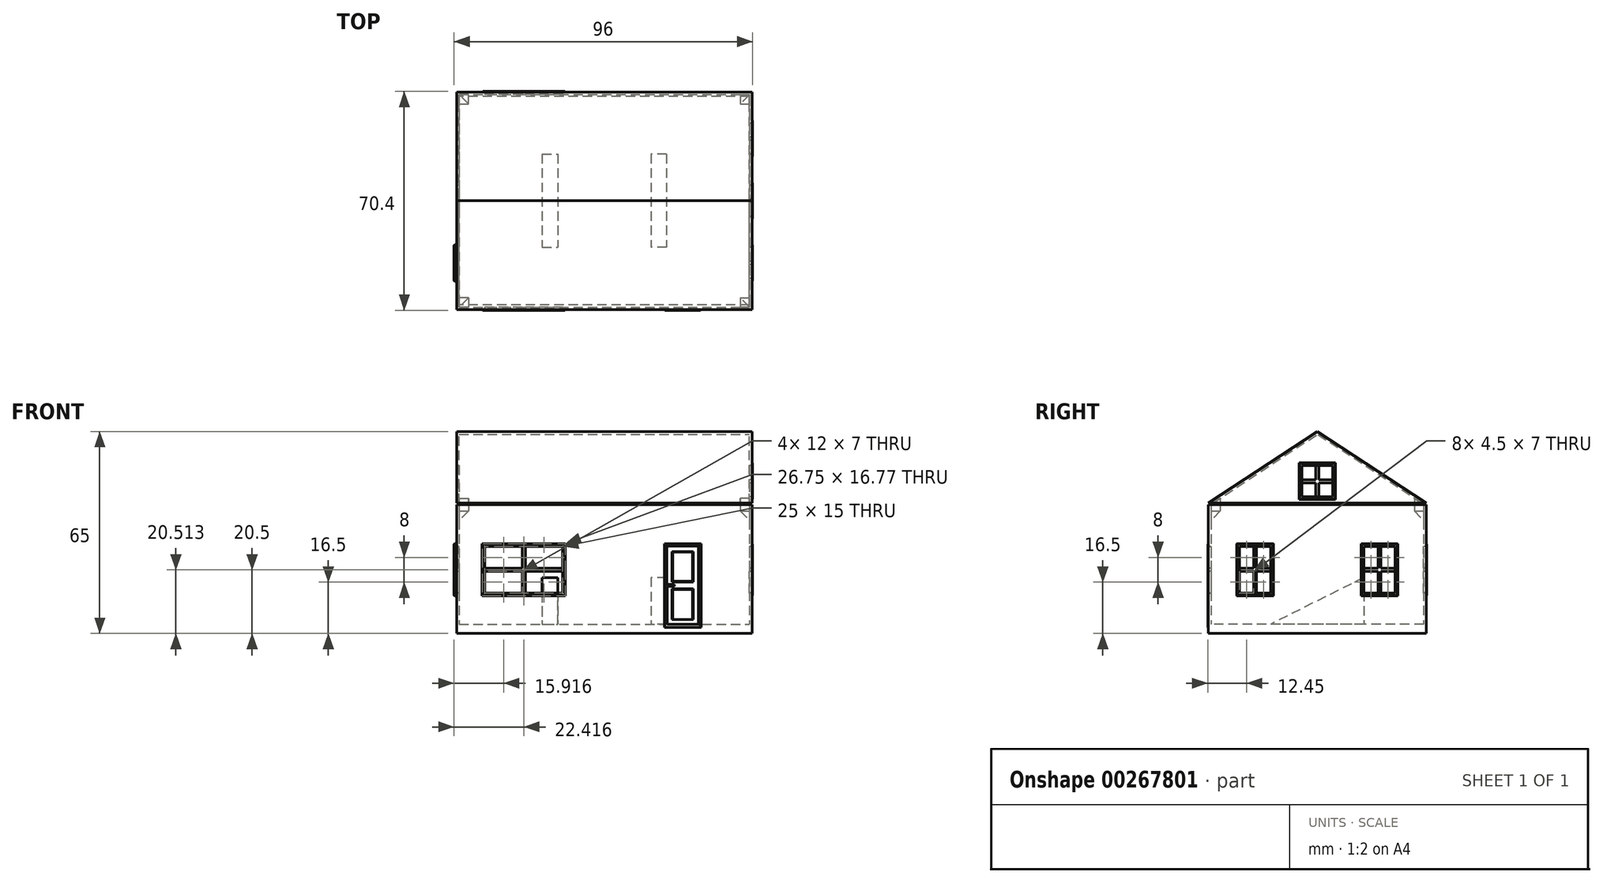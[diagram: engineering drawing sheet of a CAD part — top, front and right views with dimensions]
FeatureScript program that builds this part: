
annotation { "Feature Type Name" : "Feature", "Feature Type Description" : "" }
export const myFeature = defineFeature(function(context is Context, id is Id, definition is map)
    precondition{}
    {
        {
            var Q0;
            Q0=qCreatedBy(makeId("Top.planeOp"),FACE);
            var sketch = newSketch(context, id + "F0", { "sketchPlane" : qUnion([Q0])});
            skLineSegment(sketch, "E0.bottom", {"start": v(-47.5, 35) * mm, "end": v(47.5, 35) * mm});
            skLineSegment(sketch, "E0.top", {"start": v(-47.5, -35) * mm, "end": v(47.5, -35) * mm});
            skLineSegment(sketch, "E0.left", {"start": v(-47.5, 35) * mm, "end": v(-47.5, -35) * mm});
            skLineSegment(sketch, "E0.right", {"start": v(47.5, 35) * mm, "end": v(47.5, -35) * mm});
            skPoint(sketch, "E0.middle", {"position": v(0, 0) * mm});
            skLineSegment(sketch, "E1.bottom", {"start": v(57.5, 45) * mm, "end": v(-57.5, 45) * mm});
            skLineSegment(sketch, "E1.top", {"start": v(57.5, -45) * mm, "end": v(-57.5, -45) * mm});
            skLineSegment(sketch, "E1.left", {"start": v(57.5, 45) * mm, "end": v(57.5, -45) * mm});
            skLineSegment(sketch, "E1.right", {"start": v(-57.5, 45) * mm, "end": v(-57.5, -45) * mm});
            skLineSegment(sketch, "E2.0", {"start": v(-49.5, 37) * mm, "end": v(-49.5, -37) * mm});
            skLineSegment(sketch, "E2.1", {"start": v(-49.5, 37) * mm, "end": v(49.5, 37) * mm});
            skLineSegment(sketch, "E2.2", {"start": v(49.5, 37) * mm, "end": v(49.5, -37) * mm});
            skLineSegment(sketch, "E2.3", {"start": v(-49.5, -37) * mm, "end": v(49.5, -37) * mm});
            skSolve(sketch);
        }
        {
            var Q0;
            Q0=makeQuery(id+"F0.imprint","IMPRINT",FACE,{"disambiguationData":[TD([[makeQuery(id+"F0.imprint","IMPRINT",EDGE,{"derivedFrom":sQuery(id+"F0.wireOp",EDGE,"E0.bottom")}),-1.0]])]});
            extrude(context, id + "F1", {"entities" : qUnion([Q0]), "depth" : 65 * mm});
        }
        {
            var Q0;
            Q0=makeQuery(id+"F1.opExtrude","SWEPT_FACE",FACE,{"disambiguationData":[OSD([sQuery(id+"F0.wireOp",EDGE,"E0.left")])]});
            var sketch = newSketch(context, id + "F2", { "sketchPlane" : qUnion([Q0])});
            skLineSegment(sketch, "E3", {"start": v(0, 65) * mm, "end": v(35, 42) * mm});
            skLineSegment(sketch, "E4", {"start": v(0, 65) * mm, "end": v(0, 42.56) * mm});
            skLineSegment(sketch, "E5.MirrorCS", {"start": v(0, 65) * mm, "end": v(-35, 42) * mm});
            skLineSegment(sketch, "E6", {"start": v(-35, 42) * mm, "end": v(-35, 65) * mm});
            skLineSegment(sketch, "E7", {"start": v(-35, 65) * mm, "end": v(35, 65) * mm});
            skLineSegment(sketch, "E8", {"start": v(35, 65) * mm, "end": v(35, 42) * mm});
            skSolve(sketch);
        }
        {
            var Q0;
            Q0 = qSketchRegion(id + "F2", true);
            extrude(context, id + "F3", {"entities" : qUnion([Q0]), "operationType" : NewBodyOperationType.REMOVE, "oppositeDirection" : true, "depth" : 102.4 * mm});
        }
        {
            var Q0;
            Q0=makeQuery(id+"F1.opExtrude","SWEPT_FACE",FACE,{"disambiguationData":[OSD([sQuery(id+"F0.wireOp",EDGE,"E0.left")])]});
            var sketch = newSketch(context, id + "F4", { "sketchPlane" : qUnion([Q0])});
            skLineSegment(sketch, "E9.bottom", {"start": v(-15, 13) * mm, "end": v(-25, 13) * mm});
            skLineSegment(sketch, "E9.top", {"start": v(-15, 28) * mm, "end": v(-25, 28) * mm});
            skLineSegment(sketch, "E9.left", {"start": v(-15, 13) * mm, "end": v(-15, 28) * mm});
            skLineSegment(sketch, "E9.right", {"start": v(-25, 13) * mm, "end": v(-25, 28) * mm});
            skPoint(sketch, "E9.middle", {"position": v(-20, 20.5) * mm});
            skLineSegment(sketch, "E10.bottom", {"start": v(-19.5, 28) * mm, "end": v(-20.5, 28) * mm});
            skLineSegment(sketch, "E10.top", {"start": v(-19.5, 13) * mm, "end": v(-20.5, 13) * mm});
            skLineSegment(sketch, "E10.left", {"start": v(-19.5, 28) * mm, "end": v(-19.5, 13) * mm});
            skLineSegment(sketch, "E10.right", {"start": v(-20.5, 28) * mm, "end": v(-20.5, 13) * mm});
            skLineSegment(sketch, "E11.bottom", {"start": v(-15, 21) * mm, "end": v(-25, 21) * mm});
            skLineSegment(sketch, "E11.top", {"start": v(-15, 20) * mm, "end": v(-25, 20) * mm});
            skLineSegment(sketch, "E11.left", {"start": v(-15, 21) * mm, "end": v(-15, 20) * mm});
            skLineSegment(sketch, "E11.right", {"start": v(-25, 21) * mm, "end": v(-25, 20) * mm});
            skLineSegment(sketch, "E12.bottom", {"start": v(-14, 29) * mm, "end": v(-26, 29) * mm});
            skLineSegment(sketch, "E12.top", {"start": v(-14, 12) * mm, "end": v(-26, 12) * mm});
            skLineSegment(sketch, "E12.left", {"start": v(-14, 29) * mm, "end": v(-14, 12) * mm});
            skLineSegment(sketch, "E12.right", {"start": v(-26, 29) * mm, "end": v(-26, 12) * mm});
            skLineSegment(sketch, "E13", {"start": v(0, 65) * mm, "end": v(0, 3) * mm});
            skLineSegment(sketch, "E14.MirrorCS", {"start": v(14, 29) * mm, "end": v(26, 29) * mm});
            skLineSegment(sketch, "E15.MirrorCS", {"start": v(26, 29) * mm, "end": v(26, 12) * mm});
            skLineSegment(sketch, "E16.MirrorCS", {"start": v(25, 13) * mm, "end": v(25, 28) * mm});
            skLineSegment(sketch, "E17.MirrorCS", {"start": v(15, 21) * mm, "end": v(25, 21) * mm});
            skLineSegment(sketch, "E18.MirrorCS", {"start": v(15, 20) * mm, "end": v(25, 20) * mm});
            skLineSegment(sketch, "E19.MirrorCS", {"start": v(20.5, 28) * mm, "end": v(20.5, 13) * mm});
            skLineSegment(sketch, "E20.MirrorCS", {"start": v(15, 13) * mm, "end": v(25, 13) * mm});
            skLineSegment(sketch, "E21.MirrorCS", {"start": v(14, 12) * mm, "end": v(26, 12) * mm});
            skLineSegment(sketch, "E22.MirrorCS", {"start": v(15, 13) * mm, "end": v(15, 28) * mm});
            skLineSegment(sketch, "E23.MirrorCS", {"start": v(14, 29) * mm, "end": v(14, 12) * mm});
            skLineSegment(sketch, "E24.MirrorCS", {"start": v(15, 28) * mm, "end": v(25, 28) * mm});
            skLineSegment(sketch, "E25.MirrorCS", {"start": v(19.5, 28) * mm, "end": v(19.5, 13) * mm});
            skLineSegment(sketch, "E26.bottom", {"start": v(-5, 54) * mm, "end": v(5, 54) * mm});
            skLineSegment(sketch, "E26.top", {"start": v(-5, 44) * mm, "end": v(5, 44) * mm});
            skLineSegment(sketch, "E26.left", {"start": v(-5, 54) * mm, "end": v(-5, 44) * mm});
            skLineSegment(sketch, "E26.right", {"start": v(5, 54) * mm, "end": v(5, 44) * mm});
            skPoint(sketch, "E26.middle", {"position": v(0, 49) * mm});
            skLineSegment(sketch, "E27.bottom", {"start": v(0.5, 54) * mm, "end": v(-0.5, 54) * mm});
            skLineSegment(sketch, "E27.top", {"start": v(0.5, 44) * mm, "end": v(-0.5, 44) * mm});
            skLineSegment(sketch, "E27.left", {"start": v(0.5, 54) * mm, "end": v(0.5, 44) * mm});
            skLineSegment(sketch, "E27.right", {"start": v(-0.5, 54) * mm, "end": v(-0.5, 44) * mm});
            skLineSegment(sketch, "E28.bottom", {"start": v(5, 49.5) * mm, "end": v(-5, 49.5) * mm});
            skLineSegment(sketch, "E28.top", {"start": v(5, 48.5) * mm, "end": v(-5, 48.5) * mm});
            skLineSegment(sketch, "E28.left", {"start": v(5, 49.5) * mm, "end": v(5, 48.5) * mm});
            skLineSegment(sketch, "E28.right", {"start": v(-5, 49.5) * mm, "end": v(-5, 48.5) * mm});
            skLineSegment(sketch, "E29.bottom", {"start": v(6, 55) * mm, "end": v(-6, 55) * mm});
            skLineSegment(sketch, "E29.top", {"start": v(6, 43) * mm, "end": v(-6, 43) * mm});
            skLineSegment(sketch, "E29.left", {"start": v(6, 55) * mm, "end": v(6, 43) * mm});
            skLineSegment(sketch, "E29.right", {"start": v(-6, 55) * mm, "end": v(-6, 43) * mm});
            skSolve(sketch);
        }
        {
            var Q0;
            {var subQ0=sQuery(id+"F4.wireOp",EDGE,"E26.left");var subQ1=sQuery(id+"F4.wireOp",EDGE,"E26.bottom");var subQ2=makeQuery(id+"F4.imprint","INTERSECT",VERTEX,{"derivedFrom":[subQ1,subQ0]});Q0=makeQuery(id+"F4.imprint","IMPRINT",FACE,{"disambiguationData":[TD([[makeQuery(id+"F4.imprint","IMPRINT",EDGE,{"disambiguationData":[TD([[subQ2,-1.0]])],"derivedFrom":subQ1}),-1.0]])]});}
            var Q1;
            {var subQ0=sQuery(id+"F4.wireOp",EDGE,"E26.left");var subQ1=sQuery(id+"F4.wireOp",EDGE,"E26.top");var subQ2=makeQuery(id+"F4.imprint","INTERSECT",VERTEX,{"derivedFrom":[subQ1,subQ0]});Q1=makeQuery(id+"F4.imprint","IMPRINT",FACE,{"disambiguationData":[TD([[makeQuery(id+"F4.imprint","IMPRINT",EDGE,{"disambiguationData":[TD([[subQ2,-1.0]])],"derivedFrom":subQ1}),1.0]])]});}
            var Q2;
            {var subQ0=sQuery(id+"F4.wireOp",EDGE,"E26.right");var subQ1=sQuery(id+"F4.wireOp",EDGE,"E26.bottom");var subQ2=makeQuery(id+"F4.imprint","INTERSECT",VERTEX,{"derivedFrom":[subQ1,subQ0]});Q2=makeQuery(id+"F4.imprint","IMPRINT",FACE,{"disambiguationData":[TD([[makeQuery(id+"F4.imprint","IMPRINT",EDGE,{"disambiguationData":[TD([[subQ2,1.0]])],"derivedFrom":subQ1}),-1.0]])]});}
            var Q3;
            {var subQ0=sQuery(id+"F4.wireOp",EDGE,"E26.right");var subQ1=sQuery(id+"F4.wireOp",EDGE,"E26.top");var subQ2=makeQuery(id+"F4.imprint","INTERSECT",VERTEX,{"derivedFrom":[subQ1,subQ0]});Q3=makeQuery(id+"F4.imprint","IMPRINT",FACE,{"disambiguationData":[TD([[makeQuery(id+"F4.imprint","IMPRINT",EDGE,{"disambiguationData":[TD([[subQ2,1.0]])],"derivedFrom":subQ1}),1.0]])]});}
            var Q4;
            {var subQ0=sQuery(id+"F4.wireOp",EDGE,"E22.MirrorCS");var subQ1=sQuery(id+"F4.wireOp",EDGE,"E17.MirrorCS");var subQ2=makeQuery(id+"F4.imprint","INTERSECT",VERTEX,{"derivedFrom":[subQ1,subQ0]});Q4=makeQuery(id+"F4.imprint","IMPRINT",FACE,{"disambiguationData":[TD([[makeQuery(id+"F4.imprint","IMPRINT",EDGE,{"disambiguationData":[TD([[subQ2,-1.0]])],"derivedFrom":subQ1}),1.0]])]});}
            var Q5;
            {var subQ0=sQuery(id+"F4.wireOp",EDGE,"E24.MirrorCS");var subQ1=sQuery(id+"F4.wireOp",EDGE,"E16.MirrorCS");var subQ2=makeQuery(id+"F4.imprint","INTERSECT",VERTEX,{"derivedFrom":[subQ1,subQ0]});Q5=makeQuery(id+"F4.imprint","IMPRINT",FACE,{"disambiguationData":[TD([[makeQuery(id+"F4.imprint","IMPRINT",EDGE,{"disambiguationData":[TD([[subQ2,1.0]])],"derivedFrom":subQ1}),1.0]])]});}
            var Q6;
            {var subQ0=sQuery(id+"F4.wireOp",EDGE,"E22.MirrorCS");var subQ1=sQuery(id+"F4.wireOp",EDGE,"E18.MirrorCS");var subQ2=makeQuery(id+"F4.imprint","INTERSECT",VERTEX,{"derivedFrom":[subQ1,subQ0]});Q6=makeQuery(id+"F4.imprint","IMPRINT",FACE,{"disambiguationData":[TD([[makeQuery(id+"F4.imprint","IMPRINT",EDGE,{"disambiguationData":[TD([[subQ2,-1.0]])],"derivedFrom":subQ1}),-1.0]])]});}
            var Q7;
            {var subQ0=sQuery(id+"F4.wireOp",EDGE,"E20.MirrorCS");var subQ1=sQuery(id+"F4.wireOp",EDGE,"E16.MirrorCS");var subQ2=makeQuery(id+"F4.imprint","INTERSECT",VERTEX,{"derivedFrom":[subQ1,subQ0]});Q7=makeQuery(id+"F4.imprint","IMPRINT",FACE,{"disambiguationData":[TD([[makeQuery(id+"F4.imprint","IMPRINT",EDGE,{"disambiguationData":[TD([[subQ2,-1.0]])],"derivedFrom":subQ1}),1.0]])]});}
            var Q8;
            {var subQ0=sQuery(id+"F4.wireOp",EDGE,"E9.left");var subQ1=sQuery(id+"F4.wireOp",EDGE,"E9.bottom");var subQ2=makeQuery(id+"F4.imprint","INTERSECT",VERTEX,{"derivedFrom":[subQ1,subQ0]});Q8=makeQuery(id+"F4.imprint","IMPRINT",FACE,{"disambiguationData":[TD([[makeQuery(id+"F4.imprint","IMPRINT",EDGE,{"disambiguationData":[TD([[subQ2,-1.0]])],"derivedFrom":subQ1}),-1.0]])]});}
            var Q9;
            {var subQ0=sQuery(id+"F4.wireOp",EDGE,"E9.left");var subQ1=sQuery(id+"F4.wireOp",EDGE,"E9.top");var subQ2=makeQuery(id+"F4.imprint","INTERSECT",VERTEX,{"derivedFrom":[subQ1,subQ0]});Q9=makeQuery(id+"F4.imprint","IMPRINT",FACE,{"disambiguationData":[TD([[makeQuery(id+"F4.imprint","IMPRINT",EDGE,{"disambiguationData":[TD([[subQ2,-1.0]])],"derivedFrom":subQ1}),1.0]])]});}
            var Q10;
            {var subQ0=sQuery(id+"F4.wireOp",EDGE,"E9.right");var subQ1=sQuery(id+"F4.wireOp",EDGE,"E9.top");var subQ2=makeQuery(id+"F4.imprint","INTERSECT",VERTEX,{"derivedFrom":[subQ1,subQ0]});Q10=makeQuery(id+"F4.imprint","IMPRINT",FACE,{"disambiguationData":[TD([[makeQuery(id+"F4.imprint","IMPRINT",EDGE,{"disambiguationData":[TD([[subQ2,1.0]])],"derivedFrom":subQ1}),1.0]])]});}
            var Q11;
            {var subQ0=sQuery(id+"F4.wireOp",EDGE,"E9.right");var subQ1=sQuery(id+"F4.wireOp",EDGE,"E9.bottom");var subQ2=makeQuery(id+"F4.imprint","INTERSECT",VERTEX,{"derivedFrom":[subQ1,subQ0]});Q11=makeQuery(id+"F4.imprint","IMPRINT",FACE,{"disambiguationData":[TD([[makeQuery(id+"F4.imprint","IMPRINT",EDGE,{"disambiguationData":[TD([[subQ2,1.0]])],"derivedFrom":subQ1}),-1.0]])]});}
            extrude(context, id + "F5", {"entities" : qUnion([Q0, Q1, Q2, Q3, Q4, Q5, Q6, Q7, Q8, Q9, Q10, Q11]), "operationType" : NewBodyOperationType.REMOVE, "oppositeDirection" : true, "depth" : 139.2 * mm});
        }
        {
            var Q0;
            {var subQ9=sQuery(id+"F4.wireOp",EDGE,"E28.right");Q0=makeQuery(id+"F4.imprint","IMPRINT",FACE,{"disambiguationData":[TD([[makeQuery(id+"F4.imprint","IMPRINT",EDGE,{"derivedFrom":subQ9}),-1.0]])]});}
            var Q1;
            {var subQ0=sQuery(id+"F4.wireOp",EDGE,"E28.left");Q1=makeQuery(id+"F4.imprint","IMPRINT",FACE,{"disambiguationData":[TD([[makeQuery(id+"F4.imprint","IMPRINT",EDGE,{"derivedFrom":subQ0}),1.0]])]});}
            var Q2;
            Q2=makeQuery(id+"F4.imprint","IMPRINT",FACE,{"disambiguationData":[TD([[makeQuery(id+"F4.imprint","IMPRINT",EDGE,{"derivedFrom":sQuery(id+"F4.wireOp",EDGE,"E14.MirrorCS")}),-1.0]])]});
            var Q3;
            {var subQ1=sQuery(id+"F4.wireOp",EDGE,"E10.bottom");Q3=makeQuery(id+"F4.imprint","IMPRINT",FACE,{"disambiguationData":[TD([[makeQuery(id+"F4.imprint","IMPRINT",EDGE,{"derivedFrom":subQ1}),-1.0]])]});}
            extrude(context, id + "F6", {"entities" : qUnion([Q0, Q1, Q2, Q3]), "operationType" : NewBodyOperationType.ADD, "depth" : 0.8 * mm, "offsetDistance" : 25 * mm});
        }
        {
            var Q0;
            Q0=makeQuery(id+"F1.opExtrude","SWEPT_FACE",FACE,{"disambiguationData":[OSD([sQuery(id+"F0.wireOp",EDGE,"E0.top")])]});
            var sketch = newSketch(context, id + "F7", { "sketchPlane" : qUnion([Q0])});
            skLineSegment(sketch, "E30.bottom", {"start": v(-38.38, 28) * mm, "end": v(-13.38, 28) * mm});
            skLineSegment(sketch, "E30.top", {"start": v(-38.38, 13) * mm, "end": v(-13.38, 13) * mm});
            skLineSegment(sketch, "E30.left", {"start": v(-38.38, 28) * mm, "end": v(-38.38, 13) * mm});
            skLineSegment(sketch, "E30.right", {"start": v(-13.38, 28) * mm, "end": v(-13.38, 13) * mm});
            skPoint(sketch, "E30.middle", {"position": v(-25.88, 20.5) * mm});
            skLineSegment(sketch, "E31.bottom", {"start": v(-12.38, 29) * mm, "end": v(-39.38, 29) * mm});
            skLineSegment(sketch, "E31.top", {"start": v(-12.38, 12) * mm, "end": v(-39.38, 12) * mm});
            skLineSegment(sketch, "E31.left", {"start": v(-12.38, 29) * mm, "end": v(-12.38, 12) * mm});
            skLineSegment(sketch, "E31.right", {"start": v(-39.38, 29) * mm, "end": v(-39.38, 12) * mm});
            skLineSegment(sketch, "E32.bottom", {"start": v(-25.38, 28) * mm, "end": v(-26.38, 28) * mm});
            skLineSegment(sketch, "E32.top", {"start": v(-25.38, 13) * mm, "end": v(-26.38, 13) * mm});
            skLineSegment(sketch, "E32.left", {"start": v(-25.38, 28) * mm, "end": v(-25.38, 13) * mm});
            skLineSegment(sketch, "E32.right", {"start": v(-26.38, 28) * mm, "end": v(-26.38, 13) * mm});
            skLineSegment(sketch, "E33.bottom", {"start": v(-13.38, 21) * mm, "end": v(-38.38, 21) * mm});
            skLineSegment(sketch, "E33.top", {"start": v(-13.38, 20) * mm, "end": v(-38.38, 20) * mm});
            skLineSegment(sketch, "E33.left", {"start": v(-13.38, 21) * mm, "end": v(-13.38, 20) * mm});
            skLineSegment(sketch, "E33.right", {"start": v(-38.38, 21) * mm, "end": v(-38.38, 20) * mm});
            skLineSegment(sketch, "E34.bottom", {"start": v(30.19, 28) * mm, "end": v(20.19, 28) * mm});
            skLineSegment(sketch, "E34.top", {"start": v(30.19, 3) * mm, "end": v(20.19, 3) * mm});
            skLineSegment(sketch, "E34.left", {"start": v(30.19, 28) * mm, "end": v(30.19, 3) * mm});
            skLineSegment(sketch, "E34.right", {"start": v(20.19, 28) * mm, "end": v(20.19, 3) * mm});
            skPoint(sketch, "E34.middle", {"position": v(25.19, 15.5) * mm});
            skLineSegment(sketch, "E35.0", {"start": v(19.19, 29) * mm, "end": v(19.19, 2) * mm});
            skLineSegment(sketch, "E35.1", {"start": v(31.19, 29) * mm, "end": v(19.19, 29) * mm});
            skLineSegment(sketch, "E35.2", {"start": v(31.19, 29) * mm, "end": v(31.19, 2) * mm});
            skLineSegment(sketch, "E36.bottom", {"start": v(22.55, 15.8) * mm, "end": v(19.9, 15.8) * mm});
            skLineSegment(sketch, "E36.top", {"start": v(22.55, 15.2) * mm, "end": v(19.9, 15.2) * mm});
            skLineSegment(sketch, "E36.left", {"start": v(22.55, 15.8) * mm, "end": v(22.55, 15.2) * mm});
            skLineSegment(sketch, "E36.right", {"start": v(19.9, 15.8) * mm, "end": v(19.9, 15.2) * mm});
            skPoint(sketch, "E36.middle", {"position": v(21.22, 15.5) * mm});
            skPoint(sketch, "E36.middle.positionSnap0", {"position": v(20.19, 15.5) * mm});
            skPoint(sketch, "E36.centerSnap0", {"position": v(20.19, 15.5) * mm});
            skLineSegment(sketch, "E37.bottom", {"start": v(28.69, 26.5) * mm, "end": v(21.69, 26.5) * mm});
            skLineSegment(sketch, "E37.top", {"start": v(28.69, 16.5) * mm, "end": v(21.69, 16.5) * mm});
            skLineSegment(sketch, "E37.left", {"start": v(28.69, 26.5) * mm, "end": v(28.69, 16.5) * mm});
            skLineSegment(sketch, "E37.right", {"start": v(21.69, 26.5) * mm, "end": v(21.69, 16.5) * mm});
            skPoint(sketch, "E37.middle", {"position": v(25.19, 21.5) * mm});
            skLineSegment(sketch, "E38", {"start": v(25.19, 15.5) * mm, "end": v(27.66, 15.5) * mm});
            skLineSegment(sketch, "E39.MirrorCS", {"start": v(28.69, 14.5) * mm, "end": v(21.69, 14.5) * mm});
            skLineSegment(sketch, "E40.MirrorCS", {"start": v(21.69, 4.5) * mm, "end": v(21.69, 14.5) * mm});
            skLineSegment(sketch, "E41.MirrorCS", {"start": v(28.69, 4.5) * mm, "end": v(21.69, 4.5) * mm});
            skLineSegment(sketch, "E42.MirrorCS", {"start": v(28.69, 4.5) * mm, "end": v(28.69, 14.5) * mm});
            skLineSegment(sketch, "E43.0", {"start": v(31.19, 2) * mm, "end": v(19.19, 2) * mm});
            skSolve(sketch);
        }
        {
            var Q0;
            {var subQ5=sQuery(id+"F7.wireOp",EDGE,"E36.left");Q0=makeQuery(id+"F7.imprint","IMPRINT",FACE,{"disambiguationData":[TD([[makeQuery(id+"F7.imprint","IMPRINT",EDGE,{"derivedFrom":subQ5}),-1.0]])]});}
            var Q1;
            {var subQ5=sQuery(id+"F7.wireOp",EDGE,"E36.right");Q1=makeQuery(id+"F7.imprint","IMPRINT",FACE,{"disambiguationData":[TD([[makeQuery(id+"F7.imprint","IMPRINT",EDGE,{"derivedFrom":subQ5}),1.0]])]});}
            var Q2;
            Q2=makeQuery(id+"F7.imprint","IMPRINT",FACE,{"disambiguationData":[TD([[makeQuery(id+"F7.imprint","IMPRINT",EDGE,{"derivedFrom":sQuery(id+"F7.wireOp",EDGE,"E31.bottom")}),1.0]])]});
            var Q3;
            {var subQ11=sQuery(id+"F7.wireOp",EDGE,"E34.bottom");Q3=makeQuery(id+"F7.imprint","IMPRINT",FACE,{"disambiguationData":[TD([[makeQuery(id+"F7.imprint","IMPRINT",EDGE,{"derivedFrom":subQ11}),-1.0]])]});}
            extrude(context, id + "F8", {"entities" : qUnion([Q0, Q1, Q2, Q3]), "operationType" : NewBodyOperationType.ADD, "depth" : 0.2 * mm});
        }
        {
            var Q0;
            {var subQ0=sQuery(id+"F7.wireOp",EDGE,"E30.left");var subQ1=sQuery(id+"F7.wireOp",EDGE,"E30.bottom");var subQ2=makeQuery(id+"F7.imprint","INTERSECT",VERTEX,{"derivedFrom":[subQ1,subQ0]});Q0=makeQuery(id+"F7.imprint","IMPRINT",FACE,{"disambiguationData":[TD([[makeQuery(id+"F7.imprint","IMPRINT",EDGE,{"disambiguationData":[TD([[subQ2,-1.0]])],"derivedFrom":subQ1}),-1.0]])]});}
            var Q1;
            {var subQ0=sQuery(id+"F7.wireOp",EDGE,"E30.left");var subQ1=sQuery(id+"F7.wireOp",EDGE,"E30.top");var subQ2=makeQuery(id+"F7.imprint","INTERSECT",VERTEX,{"derivedFrom":[subQ1,subQ0]});Q1=makeQuery(id+"F7.imprint","IMPRINT",FACE,{"disambiguationData":[TD([[makeQuery(id+"F7.imprint","IMPRINT",EDGE,{"disambiguationData":[TD([[subQ2,-1.0]])],"derivedFrom":subQ1}),1.0]])]});}
            var Q2;
            {var subQ0=sQuery(id+"F7.wireOp",EDGE,"E30.right");var subQ1=sQuery(id+"F7.wireOp",EDGE,"E30.bottom");var subQ2=makeQuery(id+"F7.imprint","INTERSECT",VERTEX,{"derivedFrom":[subQ1,subQ0]});Q2=makeQuery(id+"F7.imprint","IMPRINT",FACE,{"disambiguationData":[TD([[makeQuery(id+"F7.imprint","IMPRINT",EDGE,{"disambiguationData":[TD([[subQ2,1.0]])],"derivedFrom":subQ1}),-1.0]])]});}
            var Q3;
            {var subQ0=sQuery(id+"F7.wireOp",EDGE,"E30.right");var subQ1=sQuery(id+"F7.wireOp",EDGE,"E30.top");var subQ2=makeQuery(id+"F7.imprint","INTERSECT",VERTEX,{"derivedFrom":[subQ1,subQ0]});Q3=makeQuery(id+"F7.imprint","IMPRINT",FACE,{"disambiguationData":[TD([[makeQuery(id+"F7.imprint","IMPRINT",EDGE,{"disambiguationData":[TD([[subQ2,1.0]])],"derivedFrom":subQ1}),1.0]])]});}
            extrude(context, id + "F9", {"entities" : qUnion([Q0, Q1, Q2, Q3]), "operationType" : NewBodyOperationType.REMOVE, "oppositeDirection" : true, "depth" : 74.2 * mm, "offsetDistance" : 25 * mm});
        }
        {
            var Q0;
            Q0=makeQuery(id+"F7.imprint","IMPRINT",FACE,{"disambiguationData":[TD([[makeQuery(id+"F7.imprint","IMPRINT",EDGE,{"derivedFrom":sQuery(id+"F7.wireOp",EDGE,"E37.bottom")}),1.0]])]});
            var Q1;
            Q1=makeQuery(id+"F7.imprint","IMPRINT",FACE,{"disambiguationData":[TD([[makeQuery(id+"F7.imprint","IMPRINT",EDGE,{"derivedFrom":sQuery(id+"F7.wireOp",EDGE,"E39.MirrorCS")}),1.0]])]});
            extrude(context, id + "F10", {"entities" : qUnion([Q0, Q1]), "operationType" : NewBodyOperationType.ADD, "depth" : 0.2 * mm});
        }
        {
            var Q0;
            Q0=makeQuery(id+"F1.opExtrude","SWEPT_FACE",FACE,{"disambiguationData":[OSD([sQuery(id+"F0.wireOp",EDGE,"E0.right")])]});
            var sketch = newSketch(context, id + "F11", { "sketchPlane" : qUnion([Q0])});
            skLineSegment(sketch, "E44", {"start": v(-35, 42) * mm, "end": v(35, 42) * mm});
            skSolve(sketch);
        }
        {
            var Q0;
            Q0=makeQuery(id+"F11.imprint","IMPRINT",FACE,{"disambiguationData":[TD([[makeQuery(id+"F11.imprint","IMPRINT",EDGE,{"derivedFrom":sQuery(id+"F11.wireOp",EDGE,"E44")}),-1.0]])]});
            var sketch = newSketch(context, id + "F12", { "sketchPlane" : qUnion([Q0])});
            skLineSegment(sketch, "E45.0", {"start": v(34.2, 41.57) * mm, "end": v(34.2, 3) * mm});
            skLineSegment(sketch, "E45.1", {"start": v(34.2, 41.57) * mm, "end": v(0, 64.04) * mm});
            skLineSegment(sketch, "E45.2", {"start": v(-34.2, 41.57) * mm, "end": v(0, 64.04) * mm});
            skLineSegment(sketch, "E45.3", {"start": v(-34.2, 41.57) * mm, "end": v(-34.2, 3) * mm});
            skLineSegment(sketch, "E46", {"start": v(34.2, 3) * mm, "end": v(-34.2, 3) * mm});
            skSolve(sketch);
        }
        {
            var Q0;
            {var subQ37=sQuery(id+"F12.wireOp",EDGE,"E45.0");Q0=makeQuery(id+"F12.imprint","IMPRINT",FACE,{"disambiguationData":[TD([[makeQuery(id+"F12.imprint","IMPRINT",EDGE,{"derivedFrom":subQ37}),-1.0]])]});}
            var Q1;
            {var subQ0=sQuery(id+"F12.wireOp",EDGE,"E45.2");var subQ1=sQuery(id+"F12.wireOp",EDGE,"E45.1");var subQ2=makeQuery(id+"F12.imprint","INTERSECT",VERTEX,{"derivedFrom":[subQ1,subQ0]});Q1=makeQuery(id+"F12.imprint","IMPRINT",FACE,{"disambiguationData":[TD([[makeQuery(id+"F12.imprint","IMPRINT",EDGE,{"disambiguationData":[TD([[subQ2,1.0]])],"derivedFrom":subQ1}),1.0]])]});}
            extrude(context, id + "F13", {"entities" : qUnion([Q0, Q1]), "operationType" : NewBodyOperationType.REMOVE, "oppositeDirection" : true, "depth" : 94.2 * mm, "hasSecondDirection" : true, "secondDirectionOppositeDirection" : true, "secondDirectionDepth" : 0.8 * mm});
        }
        {
            var Q0;
            Q0=makeQuery(id+"F8.opExtrude","CAP_EDGE",EDGE,{"disambiguationData":[OSD([sQuery(id+"F7.wireOp",EDGE,"E31.bottom")])],"isStart":false});
            var Q1;
            Q1=makeQuery(id+"F8.opExtrude","CAP_EDGE",EDGE,{"disambiguationData":[OSD([sQuery(id+"F7.wireOp",EDGE,"E31.right")])],"isStart":false});
            var Q2;
            Q2=makeQuery(id+"F8.opExtrude","CAP_EDGE",EDGE,{"disambiguationData":[OSD([sQuery(id+"F7.wireOp",EDGE,"E31.left")])],"isStart":false});
            var Q3;
            Q3=makeQuery(id+"F8.opExtrude","CAP_EDGE",EDGE,{"disambiguationData":[OSD([sQuery(id+"F7.wireOp",EDGE,"E31.top")])],"isStart":false});
            var Q4;
            Q4=makeQuery(id+"F8.opExtrude","CAP_EDGE",EDGE,{"disambiguationData":[OSD([sQuery(id+"F7.wireOp",EDGE,"E35.0")])],"isStart":false});
            var Q5;
            Q5=makeQuery(id+"F8.opExtrude","CAP_EDGE",EDGE,{"disambiguationData":[OSD([sQuery(id+"F7.wireOp",EDGE,"E35.1")])],"isStart":false});
            var Q6;
            Q6=makeQuery(id+"F8.opExtrude","CAP_EDGE",EDGE,{"disambiguationData":[OSD([sQuery(id+"F7.wireOp",EDGE,"E35.2")])],"isStart":false});
            var Q7;
            Q7=makeQuery(id+"F8.opExtrude","CAP_EDGE",EDGE,{"disambiguationData":[OSD([sQuery(id+"F7.wireOp",EDGE,"E34.bottom")])],"isStart":false});
            var Q8;
            {var subQ0=sQuery(id+"F7.wireOp",EDGE,"E34.right");Q8=makeQuery(id+"F8.opExtrude","CAP_EDGE",EDGE,{"disambiguationData":[OSD([subQ0]),TDD([makeQuery(id+"F7.imprint","IMPRINT",EDGE,{"disambiguationData":[TD([[makeQuery(id+"F7.imprint","INTERSECT",VERTEX,{"derivedFrom":[sQuery(id+"F7.wireOp",EDGE,"E34.bottom"),subQ0]}),-1.0]])],"derivedFrom":subQ0})])],"isStart":false});}
            var Q9;
            Q9=makeQuery(id+"F8.opExtrude","CAP_EDGE",EDGE,{"disambiguationData":[OSD([sQuery(id+"F7.wireOp",EDGE,"E34.left")])],"isStart":false});
            var Q10;
            Q10=makeQuery(id+"F10.opExtrude","CAP_EDGE",EDGE,{"disambiguationData":[OSD([sQuery(id+"F7.wireOp",EDGE,"E37.bottom")])],"isStart":false});
            var Q11;
            Q11=makeQuery(id+"F10.opExtrude","CAP_EDGE",EDGE,{"disambiguationData":[OSD([sQuery(id+"F7.wireOp",EDGE,"E37.right")])],"isStart":false});
            var Q12;
            Q12=makeQuery(id+"F10.opExtrude","CAP_EDGE",EDGE,{"disambiguationData":[OSD([sQuery(id+"F7.wireOp",EDGE,"E37.top")])],"isStart":false});
            var Q13;
            Q13=makeQuery(id+"F10.opExtrude","CAP_EDGE",EDGE,{"disambiguationData":[OSD([sQuery(id+"F7.wireOp",EDGE,"E37.left")])],"isStart":false});
            var Q14;
            Q14=makeQuery(id+"F10.opExtrude","CAP_EDGE",EDGE,{"disambiguationData":[OSD([sQuery(id+"F7.wireOp",EDGE,"E39.MirrorCS")])],"isStart":false});
            var Q15;
            Q15=makeQuery(id+"F10.opExtrude","CAP_EDGE",EDGE,{"disambiguationData":[OSD([sQuery(id+"F7.wireOp",EDGE,"E42.MirrorCS")])],"isStart":false});
            var Q16;
            Q16=makeQuery(id+"F10.opExtrude","CAP_EDGE",EDGE,{"disambiguationData":[OSD([sQuery(id+"F7.wireOp",EDGE,"E40.MirrorCS")])],"isStart":false});
            var Q17;
            Q17=makeQuery(id+"F6.opExtrude","CAP_EDGE",EDGE,{"disambiguationData":[OSD([sQuery(id+"F4.wireOp",EDGE,"E14.MirrorCS")])],"isStart":false});
            var Q18;
            Q18=makeQuery(id+"F6.opExtrude","CAP_EDGE",EDGE,{"disambiguationData":[OSD([sQuery(id+"F4.wireOp",EDGE,"E21.MirrorCS")])],"isStart":false});
            var Q19;
            Q19=makeQuery(id+"F6.opExtrude","CAP_EDGE",EDGE,{"disambiguationData":[OSD([sQuery(id+"F4.wireOp",EDGE,"E23.MirrorCS")])],"isStart":false});
            var Q20;
            Q20=makeQuery(id+"F6.opExtrude","CAP_EDGE",EDGE,{"disambiguationData":[OSD([sQuery(id+"F4.wireOp",EDGE,"E15.MirrorCS")])],"isStart":false});
            var Q21;
            Q21=makeQuery(id+"F6.opExtrude","CAP_EDGE",EDGE,{"disambiguationData":[OSD([sQuery(id+"F4.wireOp",EDGE,"E12.left")])],"isStart":false});
            var Q22;
            Q22=makeQuery(id+"F6.opExtrude","CAP_EDGE",EDGE,{"disambiguationData":[OSD([sQuery(id+"F4.wireOp",EDGE,"E12.bottom")])],"isStart":false});
            var Q23;
            Q23=makeQuery(id+"F6.opExtrude","CAP_EDGE",EDGE,{"disambiguationData":[OSD([sQuery(id+"F4.wireOp",EDGE,"E12.right")])],"isStart":false});
            var Q24;
            Q24=makeQuery(id+"F6.opExtrude","CAP_EDGE",EDGE,{"disambiguationData":[OSD([sQuery(id+"F4.wireOp",EDGE,"E12.top")])],"isStart":false});
            chamfer(context, id + "F14", {"entities" : qUnion([Q0, Q1, Q2, Q3, Q4, Q5, Q6, Q7, Q8, Q9, Q10, Q11, Q12, Q13, Q14, Q15, Q16, Q17, Q18, Q19, Q20, Q21, Q22, Q23, Q24]), "width" : 0.3 * mm, "tangentPropagation" : true});
        }
        {
            var Q0;
            Q0=makeQuery(id+"F11.imprint","IMPRINT",FACE,{"disambiguationData":[TD([[makeQuery(id+"F11.imprint","IMPRINT",EDGE,{"derivedFrom":sQuery(id+"F11.wireOp",EDGE,"E44")}),-1.0]])]});
            var sketch = newSketch(context, id + "F15", { "sketchPlane" : qUnion([Q0])});
            skLineSegment(sketch, "E47.bottom", {"start": v(-6, 55) * mm, "end": v(6, 55) * mm});
            skLineSegment(sketch, "E47.top", {"start": v(-6, 43.02) * mm, "end": v(6, 43.02) * mm});
            skLineSegment(sketch, "E47.left", {"start": v(-6, 55) * mm, "end": v(-6, 43.02) * mm});
            skLineSegment(sketch, "E47.right", {"start": v(6, 55) * mm, "end": v(6, 43.02) * mm});
            skPoint(sketch, "E47.middle", {"position": v(0, 49.01) * mm});
            skLineSegment(sketch, "E48.bottom", {"start": v(-26, 29) * mm, "end": v(-14, 29) * mm});
            skLineSegment(sketch, "E48.top", {"start": v(-26, 12.05) * mm, "end": v(-14, 12.05) * mm});
            skLineSegment(sketch, "E48.left", {"start": v(-26, 29) * mm, "end": v(-26, 12.05) * mm});
            skLineSegment(sketch, "E48.right", {"start": v(-14, 29) * mm, "end": v(-14, 12.05) * mm});
            skPoint(sketch, "E48.middle", {"position": v(-20, 20.53) * mm});
            skLineSegment(sketch, "E49.bottom", {"start": v(14, 29.02) * mm, "end": v(26, 29.02) * mm});
            skLineSegment(sketch, "E49.top", {"start": v(14, 12) * mm, "end": v(26, 12) * mm});
            skLineSegment(sketch, "E49.left", {"start": v(14, 29.02) * mm, "end": v(14, 12) * mm});
            skLineSegment(sketch, "E49.right", {"start": v(26, 29.02) * mm, "end": v(26, 12) * mm});
            skPoint(sketch, "E49.middle", {"position": v(20, 20.51) * mm});
            skLineSegment(sketch, "E50.0", {"start": v(-5, 54) * mm, "end": v(-5, 44.02) * mm});
            skLineSegment(sketch, "E50.1", {"start": v(-5, 54) * mm, "end": v(5, 54) * mm});
            skLineSegment(sketch, "E50.2", {"start": v(5, 54) * mm, "end": v(5, 44.02) * mm});
            skLineSegment(sketch, "E50.3", {"start": v(-5, 44.02) * mm, "end": v(5, 44.02) * mm});
            skLineSegment(sketch, "E51.0", {"start": v(-25, 28) * mm, "end": v(-15, 28) * mm});
            skLineSegment(sketch, "E51.1", {"start": v(-25, 28) * mm, "end": v(-25, 13.05) * mm});
            skLineSegment(sketch, "E51.2", {"start": v(-25, 13.05) * mm, "end": v(-15, 13.05) * mm});
            skLineSegment(sketch, "E51.3", {"start": v(-15, 28) * mm, "end": v(-15, 13.05) * mm});
            skLineSegment(sketch, "E52.0", {"start": v(15, 28.02) * mm, "end": v(15, 13) * mm});
            skLineSegment(sketch, "E52.1", {"start": v(15, 28.02) * mm, "end": v(25, 28.02) * mm});
            skLineSegment(sketch, "E52.2", {"start": v(25, 28.02) * mm, "end": v(25, 13) * mm});
            skLineSegment(sketch, "E52.3", {"start": v(15, 13) * mm, "end": v(25, 13) * mm});
            skLineSegment(sketch, "E53.0", {"start": v(-35, 41.5) * mm, "end": v(35, 41.5) * mm});
            skLineSegment(sketch, "E54", {"start": v(-35, 41.5) * mm, "end": v(-35, 42) * mm});
            skLineSegment(sketch, "E55", {"start": v(-35, 42) * mm, "end": v(35, 42) * mm});
            skLineSegment(sketch, "E56", {"start": v(35, 42) * mm, "end": v(35, 41.5) * mm});
            skSolve(sketch);
        }
        {
            var Q0;
            Q0 = qSketchRegion(id + "F15", true);
            extrude(context, id + "F16", {"entities" : qUnion([Q0]), "operationType" : NewBodyOperationType.ADD, "depth" : 0.2 * mm});
        }
        {
            var Q0;
            Q0=makeQuery(id+"F1.opExtrude","SWEPT_FACE",FACE,{"disambiguationData":[OSD([sQuery(id+"F0.wireOp",EDGE,"E0.bottom")])]});
            var sketch = newSketch(context, id + "F17", { "sketchPlane" : qUnion([Q0])});
            skLineSegment(sketch, "E57.bottom", {"start": v(12.4, 29) * mm, "end": v(39.36, 29) * mm});
            skLineSegment(sketch, "E57.top", {"start": v(12.4, 12.03) * mm, "end": v(39.36, 12.03) * mm});
            skLineSegment(sketch, "E57.left", {"start": v(12.4, 29) * mm, "end": v(12.4, 12.03) * mm});
            skLineSegment(sketch, "E57.right", {"start": v(39.36, 29) * mm, "end": v(39.36, 12.03) * mm});
            skPoint(sketch, "E57.middle", {"position": v(25.88, 20.51) * mm});
            skLineSegment(sketch, "E58.0", {"start": v(13.4, 28) * mm, "end": v(13.4, 13.03) * mm});
            skLineSegment(sketch, "E58.1", {"start": v(13.4, 28) * mm, "end": v(38.36, 28) * mm});
            skLineSegment(sketch, "E58.2", {"start": v(38.36, 28) * mm, "end": v(38.36, 13.03) * mm});
            skLineSegment(sketch, "E58.3", {"start": v(13.4, 13.03) * mm, "end": v(38.36, 13.03) * mm});
            skSolve(sketch);
        }
        {
            var Q0;
            Q0=makeQuery(id+"F17.imprint","IMPRINT",FACE,{"disambiguationData":[TD([[makeQuery(id+"F17.imprint","IMPRINT",EDGE,{"derivedFrom":sQuery(id+"F17.wireOp",EDGE,"E57.bottom")}),-1.0]])]});
            extrude(context, id + "F18", {"entities" : qUnion([Q0]), "operationType" : NewBodyOperationType.ADD, "depth" : 0.2 * mm});
        }
        {
            var Q0;
            Q0=makeQuery(id+"F18.opExtrude","CAP_EDGE",EDGE,{"disambiguationData":[OSD([sQuery(id+"F17.wireOp",EDGE,"E57.left")])],"isStart":false});
            var Q1;
            Q1=makeQuery(id+"F18.opExtrude","CAP_EDGE",EDGE,{"disambiguationData":[OSD([sQuery(id+"F17.wireOp",EDGE,"E57.bottom")])],"isStart":false});
            var Q2;
            Q2=makeQuery(id+"F18.opExtrude","CAP_EDGE",EDGE,{"disambiguationData":[OSD([sQuery(id+"F17.wireOp",EDGE,"E57.right")])],"isStart":false});
            var Q3;
            Q3=makeQuery(id+"F18.opExtrude","CAP_EDGE",EDGE,{"disambiguationData":[OSD([sQuery(id+"F17.wireOp",EDGE,"E57.top")])],"isStart":false});
            var Q4;
            Q4=makeQuery(id+"F16.opExtrude","CAP_EDGE",EDGE,{"disambiguationData":[OSD([sQuery(id+"F15.wireOp",EDGE,"E49.bottom")])],"isStart":false});
            var Q5;
            Q5=makeQuery(id+"F16.opExtrude","CAP_EDGE",EDGE,{"disambiguationData":[OSD([sQuery(id+"F15.wireOp",EDGE,"E49.left")])],"isStart":false});
            var Q6;
            Q6=makeQuery(id+"F16.opExtrude","CAP_EDGE",EDGE,{"disambiguationData":[OSD([sQuery(id+"F15.wireOp",EDGE,"E49.right")])],"isStart":false});
            var Q7;
            Q7=makeQuery(id+"F16.opExtrude","CAP_EDGE",EDGE,{"disambiguationData":[OSD([sQuery(id+"F15.wireOp",EDGE,"E49.top")])],"isStart":false});
            var Q8;
            Q8=makeQuery(id+"F16.opExtrude","CAP_EDGE",EDGE,{"disambiguationData":[OSD([sQuery(id+"F15.wireOp",EDGE,"E48.top")])],"isStart":false});
            var Q9;
            Q9=makeQuery(id+"F16.opExtrude","CAP_EDGE",EDGE,{"disambiguationData":[OSD([sQuery(id+"F15.wireOp",EDGE,"E48.left")])],"isStart":false});
            var Q10;
            Q10=makeQuery(id+"F16.opExtrude","CAP_EDGE",EDGE,{"disambiguationData":[OSD([sQuery(id+"F15.wireOp",EDGE,"E48.right")])],"isStart":false});
            var Q11;
            Q11=makeQuery(id+"F16.opExtrude","CAP_EDGE",EDGE,{"disambiguationData":[OSD([sQuery(id+"F15.wireOp",EDGE,"E48.bottom")])],"isStart":false});
            var Q12;
            Q12=makeQuery(id+"F16.opExtrude","CAP_EDGE",EDGE,{"disambiguationData":[OSD([sQuery(id+"F15.wireOp",EDGE,"E47.bottom")])],"isStart":false});
            var Q13;
            Q13=makeQuery(id+"F16.opExtrude","CAP_EDGE",EDGE,{"disambiguationData":[OSD([sQuery(id+"F15.wireOp",EDGE,"E47.left")])],"isStart":false});
            var Q14;
            Q14=makeQuery(id+"F16.opExtrude","CAP_EDGE",EDGE,{"disambiguationData":[OSD([sQuery(id+"F15.wireOp",EDGE,"E47.right")])],"isStart":false});
            var Q15;
            Q15=makeQuery(id+"F16.opExtrude","CAP_EDGE",EDGE,{"disambiguationData":[OSD([sQuery(id+"F15.wireOp",EDGE,"E47.top")])],"isStart":false});
            var Q16;
            Q16=makeQuery(id+"F0HIXgnvV618dWm_1.opExtrude","CAP_EDGE",EDGE,{"disambiguationData":[OSD([sQuery(id+"F0.wireOp",EDGE,"E1.left")])],"isStart":false});
            var Q17;
            Q17=makeQuery(id+"F0HIXgnvV618dWm_1.opExtrude","CAP_EDGE",EDGE,{"disambiguationData":[OSD([sQuery(id+"F0.wireOp",EDGE,"E1.top")])],"isStart":false});
            var Q18;
            Q18=makeQuery(id+"F0HIXgnvV618dWm_1.opExtrude","SWEPT_EDGE",EDGE,{"disambiguationData":[OSD([sQuery(id+"F0.wireOp",EDGE,"E1.top"),sQuery(id+"F0.wireOp",EDGE,"E1.left")])]});
            var Q19;
            Q19=makeQuery(id+"F0HIXgnvV618dWm_1.opExtrude","SWEPT_EDGE",EDGE,{"disambiguationData":[OSD([sQuery(id+"F0.wireOp",EDGE,"E1.top"),sQuery(id+"F0.wireOp",EDGE,"E1.right")])]});
            var Q20;
            Q20=makeQuery(id+"F0HIXgnvV618dWm_1.opExtrude","CAP_EDGE",EDGE,{"disambiguationData":[OSD([sQuery(id+"F0.wireOp",EDGE,"E1.right")])],"isStart":false});
            var Q21;
            Q21=makeQuery(id+"F0HIXgnvV618dWm_1.opExtrude","SWEPT_EDGE",EDGE,{"disambiguationData":[OSD([sQuery(id+"F0.wireOp",EDGE,"E1.bottom"),sQuery(id+"F0.wireOp",EDGE,"E1.right")])]});
            var Q22;
            Q22=makeQuery(id+"F0HIXgnvV618dWm_1.opExtrude","CAP_EDGE",EDGE,{"disambiguationData":[OSD([sQuery(id+"F0.wireOp",EDGE,"E1.bottom")])],"isStart":false});
            chamfer(context, id + "F19", {"entities" : qUnion([Q0, Q1, Q2, Q3, Q4, Q5, Q6, Q7, Q8, Q9, Q10, Q11, Q12, Q13, Q14, Q15, Q16, Q17, Q18, Q19, Q20, Q21, Q22]), "width" : 0.3 * mm, "tangentPropagation" : true});
        }
        {
            var Q0;
            Q0=makeQuery(id+"F16.opExtrude","CAP_FACE",FACE,{"disambiguationData":[OSD([sQuery(id+"F15.wireOp",EDGE,"E53.0"),sQuery(id+"F15.wireOp",EDGE,"E54"),sQuery(id+"F15.wireOp",EDGE,"E55"),sQuery(id+"F15.wireOp",EDGE,"E56")])],"isStart":false});
            extrude(context, id + "F20", {"entities" : qUnion([Q0]), "operationType" : NewBodyOperationType.REMOVE, "oppositeDirection" : true, "depth" : 99 * mm});
        }
        {
            var Q0;
            Q0=makeQuery(id+"F20.boolean.opBoolean","COPY",FACE,{"derivedFrom":makeQuery(id+"F20.opExtrude","SWEPT_FACE",FACE,{"disambiguationData":[OSD([sQuery(id+"F15.wireOp",EDGE,"E53.0")])]})});
            var sketch = newSketch(context, id + "F21", { "sketchPlane" : qUnion([Q0])});
            skLineSegment(sketch, "E59.bottom", {"start": v(-46.7, 34.2) * mm, "end": v(-43.7, 34.2) * mm});
            skLineSegment(sketch, "E59.top", {"start": v(-46.7, 31.2) * mm, "end": v(-43.7, 31.2) * mm});
            skLineSegment(sketch, "E59.left", {"start": v(-46.7, 34.2) * mm, "end": v(-46.7, 31.2) * mm});
            skLineSegment(sketch, "E59.right", {"start": v(-43.7, 34.2) * mm, "end": v(-43.7, 31.2) * mm});
            skLineSegment(sketch, "E60", {"start": v(0, 34.2) * mm, "end": v(0, 27.6) * mm});
            skPoint(sketch, "E60.endSnap0", {"position": v(0, 34.2) * mm});
            skLineSegment(sketch, "E61", {"start": v(-46.7, 0) * mm, "end": v(-36.2, 0) * mm});
            skPoint(sketch, "E61.endSnap0", {"position": v(-46.7, 0) * mm});
            skLineSegment(sketch, "E62.MirrorCS", {"start": v(43.7, 34.2) * mm, "end": v(43.7, 31.2) * mm});
            skLineSegment(sketch, "E63.MirrorCS", {"start": v(46.7, 31.2) * mm, "end": v(43.7, 31.2) * mm});
            skLineSegment(sketch, "E64.MirrorCS", {"start": v(46.7, 34.2) * mm, "end": v(46.7, 31.2) * mm});
            skLineSegment(sketch, "E65.MirrorCS", {"start": v(46.7, 34.2) * mm, "end": v(43.7, 34.2) * mm});
            skLineSegment(sketch, "E66.MirrorCS", {"start": v(-46.7, -31.2) * mm, "end": v(-43.7, -31.2) * mm});
            skLineSegment(sketch, "E67.MirrorCS", {"start": v(-43.7, -34.2) * mm, "end": v(-43.7, -31.2) * mm});
            skLineSegment(sketch, "E68.MirrorCS", {"start": v(-46.7, -34.2) * mm, "end": v(-46.7, -31.2) * mm});
            skLineSegment(sketch, "E69.MirrorCS", {"start": v(-46.7, -34.2) * mm, "end": v(-43.7, -34.2) * mm});
            skLineSegment(sketch, "E70.MirrorCS", {"start": v(43.7, -34.2) * mm, "end": v(43.7, -31.2) * mm});
            skLineSegment(sketch, "E71.MirrorCS", {"start": v(46.7, -34.2) * mm, "end": v(43.7, -34.2) * mm});
            skLineSegment(sketch, "E72.MirrorCS", {"start": v(46.7, -34.2) * mm, "end": v(46.7, -31.2) * mm});
            skLineSegment(sketch, "E73.MirrorCS", {"start": v(46.7, -31.2) * mm, "end": v(43.7, -31.2) * mm});
            skSolve(sketch);
        }
        {
            var Q0;
            Q0=makeQuery(id+"F21.imprint","IMPRINT",FACE,{"disambiguationData":[TD([[makeQuery(id+"F21.imprint","IMPRINT",EDGE,{"derivedFrom":sQuery(id+"F21.wireOp",EDGE,"E62.MirrorCS")}),1.0]])]});
            var Q1;
            Q1=makeQuery(id+"F21.imprint","IMPRINT",FACE,{"disambiguationData":[TD([[makeQuery(id+"F21.imprint","IMPRINT",EDGE,{"derivedFrom":sQuery(id+"F21.wireOp",EDGE,"E59.bottom")}),-1.0]])]});
            var Q2;
            Q2=makeQuery(id+"F13.boolean.opBoolean","COPY",FACE,{"derivedFrom":makeQuery(id+"F13.opExtrude","SWEPT_FACE",FACE,{"disambiguationData":[OSD([sQuery(id+"F12.wireOp",EDGE,"E45.1")])]})});
            extrude(context, id + "F22", {"entities" : qUnion([Q0, Q1]), "operationType" : NewBodyOperationType.ADD, "endBound" : BoundingType.UP_TO_SURFACE, "endBoundEntityFace" : qUnion([Q2]), "depth" : 3 * mm, "hasSecondDirection" : true, "secondDirectionOppositeDirection" : true, "secondDirectionDepth" : 5 * mm, "hasOffset" : true, "offsetDistance" : 0.1 * mm});
        }
        {
            var Q0;
            Q0=makeQuery(id+"F22.opExtrude","CAP_EDGE",EDGE,{"disambiguationData":[OSD([sQuery(id+"F21.wireOp",EDGE,"E59.right")])],"isStart":true});
            var Q1;
            Q1=makeQuery(id+"F22.opExtrude","CAP_EDGE",EDGE,{"disambiguationData":[OSD([sQuery(id+"F21.wireOp",EDGE,"E59.top")])],"isStart":true});
            var Q2;
            Q2=makeQuery(id+"F22.opExtrude","CAP_EDGE",EDGE,{"disambiguationData":[OSD([sQuery(id+"F21.wireOp",EDGE,"E63.MirrorCS")])],"isStart":true});
            var Q3;
            Q3=makeQuery(id+"F22.opExtrude","CAP_EDGE",EDGE,{"disambiguationData":[OSD([sQuery(id+"F21.wireOp",EDGE,"E62.MirrorCS")])],"isStart":true});
            var Q4;
            Q4=makeQuery(id+"F22.opExtrude","CAP_EDGE",EDGE,{"disambiguationData":[OSD([sQuery(id+"F21.wireOp",EDGE,"E73.MirrorCS")])],"isStart":true});
            var Q5;
            Q5=makeQuery(id+"F22.opExtrude","CAP_EDGE",EDGE,{"disambiguationData":[OSD([sQuery(id+"F21.wireOp",EDGE,"E70.MirrorCS")])],"isStart":true});
            var Q6;
            Q6=makeQuery(id+"F22.opExtrude","CAP_EDGE",EDGE,{"disambiguationData":[OSD([sQuery(id+"F21.wireOp",EDGE,"E66.MirrorCS")])],"isStart":true});
            var Q7;
            Q7=makeQuery(id+"F22.opExtrude","CAP_EDGE",EDGE,{"disambiguationData":[OSD([sQuery(id+"F21.wireOp",EDGE,"E67.MirrorCS")])],"isStart":true});
            chamfer(context, id + "F23", {"entities" : qUnion([Q0, Q1, Q2, Q3, Q4, Q5, Q6, Q7]), "width" : 2.9 * mm, "tangentPropagation" : true});
        }
        {
            var Q0;
            Q0=makeQuery(id+"F13.boolean.opBoolean","COPY",FACE,{"derivedFrom":makeQuery(id+"F13.opExtrude","SWEPT_FACE",FACE,{"disambiguationData":[OSD([sQuery(id+"F12.wireOp",EDGE,"E46")])]})});
            var sketch = newSketch(context, id + "F24", { "sketchPlane" : qUnion([Q0])});
            skLineSegment(sketch, "E74.bottom", {"start": v(-20, 15) * mm, "end": v(-15, 15) * mm});
            skLineSegment(sketch, "E74.top", {"start": v(-20, -15) * mm, "end": v(-15, -15) * mm});
            skLineSegment(sketch, "E74.left", {"start": v(-20, 15) * mm, "end": v(-20, -15) * mm});
            skLineSegment(sketch, "E74.right", {"start": v(-15, 15) * mm, "end": v(-15, -15) * mm});
            skLineSegment(sketch, "E75", {"start": v(0, 0) * mm, "end": v(0, 15.17) * mm});
            skLineSegment(sketch, "E76.MirrorCS", {"start": v(15, 15) * mm, "end": v(15, -15) * mm});
            skLineSegment(sketch, "E77.MirrorCS", {"start": v(20, 15) * mm, "end": v(15, 15) * mm});
            skLineSegment(sketch, "E78.MirrorCS", {"start": v(20, 15) * mm, "end": v(20, -15) * mm});
            skLineSegment(sketch, "E79.MirrorCS", {"start": v(20, -15) * mm, "end": v(15, -15) * mm});
            skSolve(sketch);
        }
        {
            var Q0;
            Q0=makeQuery(id+"F24.imprint","IMPRINT",FACE,{"disambiguationData":[TD([[makeQuery(id+"F24.imprint","IMPRINT",EDGE,{"derivedFrom":sQuery(id+"F24.wireOp",EDGE,"E74.bottom")}),-1.0]])]});
            var Q1;
            Q1=makeQuery(id+"F24.imprint","IMPRINT",FACE,{"disambiguationData":[TD([[makeQuery(id+"F24.imprint","IMPRINT",EDGE,{"derivedFrom":sQuery(id+"F24.wireOp",EDGE,"E76.MirrorCS")}),1.0]])]});
            extrude(context, id + "F25", {"entities" : qUnion([Q0, Q1]), "operationType" : NewBodyOperationType.ADD, "depth" : 15 * mm});
        }
        {
            var Q0;
            Q0=makeQuery(id+"F25.opExtrude","SWEPT_FACE",FACE,{"disambiguationData":[OSD([sQuery(id+"F24.wireOp",EDGE,"E74.left")])]});
            var sketch = newSketch(context, id + "F26", { "sketchPlane" : qUnion([Q0])});
            skLineSegment(sketch, "E80", {"start": v(-15, 18) * mm, "end": v(15, 3) * mm});
            skLineSegment(sketch, "E81", {"start": v(15, 3) * mm, "end": v(15, 18) * mm});
            skLineSegment(sketch, "E82", {"start": v(15, 18) * mm, "end": v(-15, 18) * mm});
            skSolve(sketch);
        }
        {
            var Q0;
            Q0=makeQuery(id+"F26.imprint","IMPRINT",FACE,{"disambiguationData":[TD([[makeQuery(id+"F26.imprint","IMPRINT",EDGE,{"derivedFrom":sQuery(id+"F26.wireOp",EDGE,"E80")}),1.0]])]});
            extrude(context, id + "F27", {"entities" : qUnion([Q0]), "operationType" : NewBodyOperationType.REMOVE, "oppositeDirection" : true, "depth" : 42.3 * mm, "offsetDistance" : 25 * mm});
        }
        {
            var Q0;
            Q0=makeQuery(id+"F25.opExtrude","SWEPT_FACE",FACE,{"disambiguationData":[OSD([sQuery(id+"F24.wireOp",EDGE,"E74.left")])]});
            var sketch = newSketch(context, id + "F28", { "sketchPlane" : qUnion([Q0])});
            skLineSegment(sketch, "E83", {"start": v(-15, 18) * mm, "end": v(15, 3) * mm});
            skLineSegment(sketch, "E84", {"start": v(15, 3) * mm, "end": v(15, 18) * mm});
            skLineSegment(sketch, "E85", {"start": v(15, 18) * mm, "end": v(-15, 18) * mm});
            skSolve(sketch);
        }
        {
            var Q0;
            Q0=makeQuery(id+"F28.imprint","IMPRINT",FACE,{"disambiguationData":[TD([[makeQuery(id+"F28.imprint","IMPRINT",EDGE,{"derivedFrom":sQuery(id+"F28.wireOp",EDGE,"E83")}),1.0]])]});
            extrude(context, id + "F29", {"entities" : qUnion([Q0]), "operationType" : NewBodyOperationType.REMOVE, "oppositeDirection" : true, "depth" : 44 * mm, "offsetDistance" : 25 * mm});
        }
        {
            var Q0;
            Q0=makeQuery(id+"F21.imprint","IMPRINT",FACE,{"disambiguationData":[TD([[makeQuery(id+"F21.imprint","IMPRINT",EDGE,{"derivedFrom":sQuery(id+"F21.wireOp",EDGE,"E70.MirrorCS")}),-1.0]])]});
            var Q1;
            Q1=makeQuery(id+"F21.imprint","IMPRINT",FACE,{"disambiguationData":[TD([[makeQuery(id+"F21.imprint","IMPRINT",EDGE,{"derivedFrom":sQuery(id+"F21.wireOp",EDGE,"E66.MirrorCS")}),-1.0]])]});
            var Q2;
            Q2=makeQuery(id+"F13.boolean.opBoolean","COPY",FACE,{"derivedFrom":makeQuery(id+"F13.opExtrude","SWEPT_FACE",FACE,{"disambiguationData":[OSD([sQuery(id+"F12.wireOp",EDGE,"E45.2")])]})});
            extrude(context, id + "F30", {"entities" : qUnion([Q0, Q1]), "operationType" : NewBodyOperationType.ADD, "endBound" : BoundingType.UP_TO_SURFACE, "depth" : 25 * mm, "endBoundEntityFace" : qUnion([Q2]), "hasOffset" : true, "offsetDistance" : 0.1 * mm, "hasSecondDirection" : true, "secondDirectionOppositeDirection" : true, "secondDirectionDepth" : 5 * mm});
        }
        {
            var Q0;
            Q0=makeQuery(id+"F30.opExtrude","CAP_EDGE",EDGE,{"disambiguationData":[OSD([sQuery(id+"F21.wireOp",EDGE,"E70.MirrorCS")])],"isStart":true});
            var Q1;
            Q1=makeQuery(id+"F30.opExtrude","CAP_EDGE",EDGE,{"disambiguationData":[OSD([sQuery(id+"F21.wireOp",EDGE,"E73.MirrorCS")])],"isStart":true});
            var Q2;
            Q2=makeQuery(id+"F30.opExtrude","CAP_EDGE",EDGE,{"disambiguationData":[OSD([sQuery(id+"F21.wireOp",EDGE,"E66.MirrorCS")])],"isStart":true});
            var Q3;
            Q3=makeQuery(id+"F30.opExtrude","CAP_EDGE",EDGE,{"disambiguationData":[OSD([sQuery(id+"F21.wireOp",EDGE,"E67.MirrorCS")])],"isStart":true});
            chamfer(context, id + "F31", {"entities" : qUnion([Q0, Q1, Q2, Q3]), "width" : 2.9 * mm, "tangentPropagation" : true});
        }
    });
